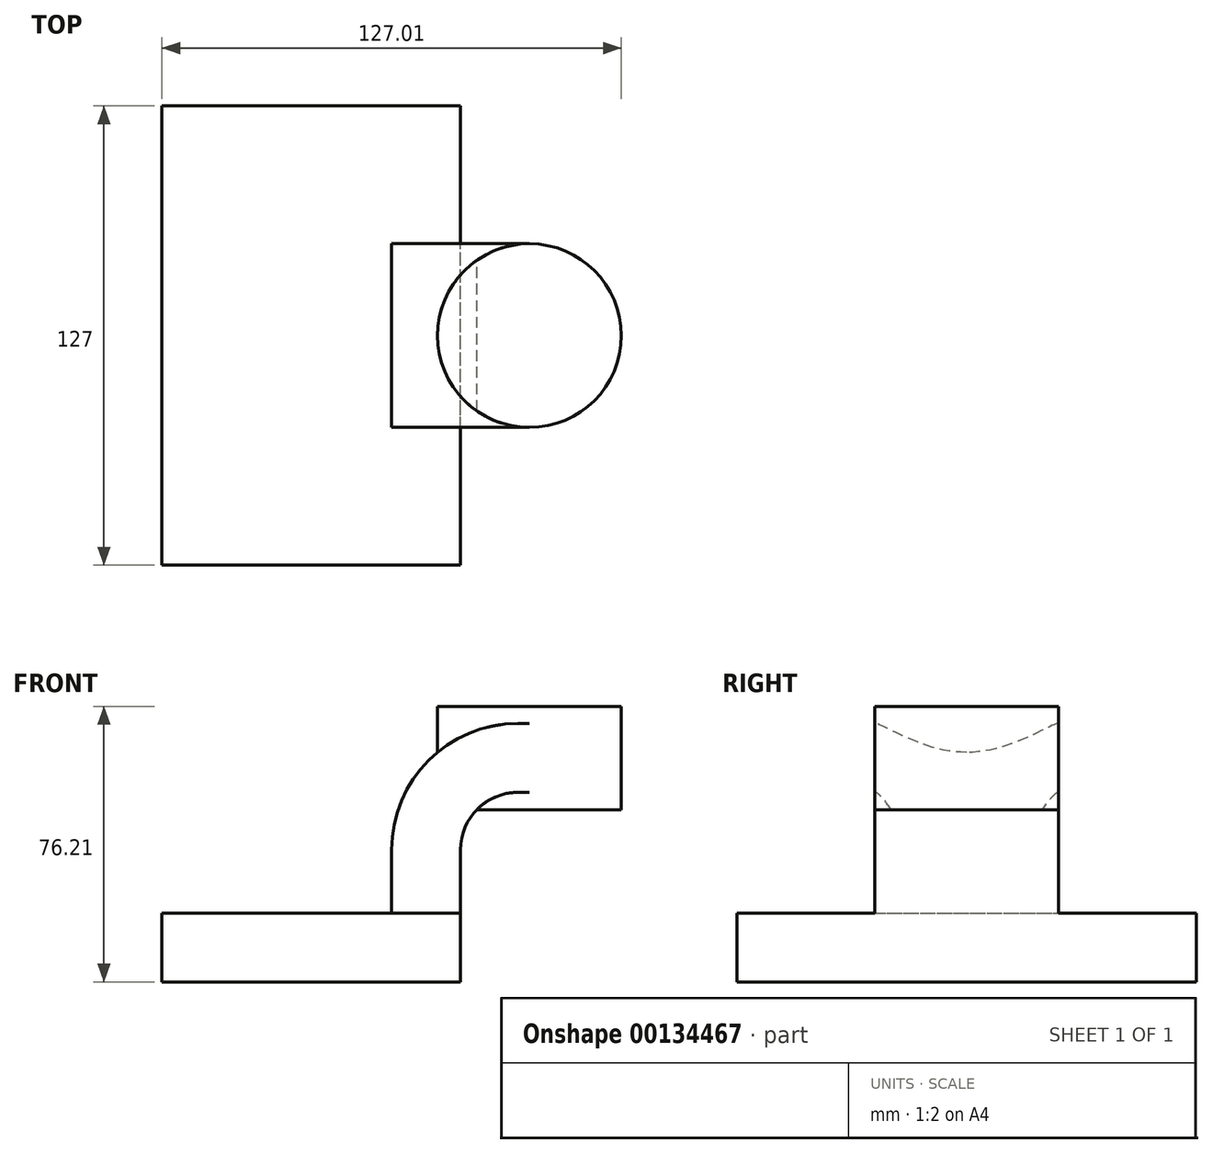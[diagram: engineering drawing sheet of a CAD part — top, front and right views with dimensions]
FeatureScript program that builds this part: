
annotation { "Feature Type Name" : "Feature", "Feature Type Description" : "" }
export const myFeature = defineFeature(function(context is Context, id is Id, definition is map)
    precondition{}
    {
        {
            var Q0;
            Q0=qCreatedBy(makeId("Front.planeOp"),FACE);
            var sketch = newSketch(context, id + "F0", { "sketchPlane" : qUnion([Q0])});
            skLineSegment(sketch, "E0.bottom", {"start": v(41.28, -9.53) * mm, "end": v(-41.28, -9.53) * mm});
            skLineSegment(sketch, "E0.top", {"start": v(41.27, 9.53) * mm, "end": v(-41.28, 9.53) * mm});
            skLineSegment(sketch, "E0.left", {"start": v(41.27, -9.53) * mm, "end": v(41.27, 9.53) * mm});
            skLineSegment(sketch, "E0.right", {"start": v(-41.28, -9.53) * mm, "end": v(-41.28, 9.52) * mm});
            skPoint(sketch, "E0.middle", {"position": v(0, 0) * mm});
            skLineSegment(sketch, "E1.bottom", {"start": v(111.12, 38.1) * mm, "end": v(60.33, 38.1) * mm});
            skLineSegment(sketch, "E1.top", {"start": v(111.12, 66.68) * mm, "end": v(60.33, 66.68) * mm});
            skLineSegment(sketch, "E1.left", {"start": v(111.13, 38.1) * mm, "end": v(111.13, 66.68) * mm});
            skLineSegment(sketch, "E1.right", {"start": v(60.33, 38.1) * mm, "end": v(60.33, 66.68) * mm});
            skLineSegment(sketch, "E2", {"start": v(41.27, 9.53) * mm, "end": v(41.27, 27) * mm});
            skArc(sketch, "E3", {"start": v(41.27, 27) * mm, "mid": v(45.92, 38.23) * mm, "end": v(57.15, 42.88) * mm});
            skLineSegment(sketch, "E4", {"start": v(57.15, 42.88) * mm, "end": v(85.73, 42.88) * mm});
            skLineSegment(sketch, "E5.0", {"start": v(57.15, 61.93) * mm, "end": v(85.72, 61.93) * mm});
            skArc(sketch, "E5.1", {"start": v(22.22, 27) * mm, "mid": v(32.45, 51.7) * mm, "end": v(57.15, 61.93) * mm});
            skLineSegment(sketch, "E6.0", {"start": v(22.22, 9.53) * mm, "end": v(22.22, 27) * mm});
            skFitSpline(sketch, "E7", {"points": [v(-41.28, 9.52) * mm, v(57.15, 61.93) * mm], "startDerivative": vector(-1.37, 29.96) * mm, "endDerivative": vector(193.18, -12.27) * mm});
            skLineSegment(sketch, "E8", {"start": v(85.72, 66.68) * mm, "end": v(85.72, 38.1) * mm});
            skSolve(sketch);
        }
        {
            var Q0;
            Q0=makeQuery(id+"F0.imprint","IMPRINT",FACE,{"disambiguationData":[TD([[makeQuery(id+"F0.imprint","IMPRINT",EDGE,{"derivedFrom":sQuery(id+"F0.wireOp",EDGE,"E0.bottom")}),-1.0]])]});
            extrude(context, id + "F1", {"entities" : qUnion([Q0]), "endBound" : BoundingType.SYMMETRIC, "depth" : 127 * mm});
        }
        {
            var Q0;
            {var subQ2=sQuery(id+"F0.wireOp",EDGE,"E2");Q0=makeQuery(id+"F0.imprint","IMPRINT",FACE,{"disambiguationData":[TD([[makeQuery(id+"F0.imprint","IMPRINT",EDGE,{"derivedFrom":subQ2}),1.0]])]});}
            var Q1;
            {var subQ5=sQuery(id+"F0.wireOp",EDGE,"xmvg7gtr-0cF6-FCa6-2jLr-h9ZZnqTFkXLl");Q1=makeQuery(id+"F0.imprint","IMPRINT",FACE,{"disambiguationData":[TD([[makeQuery(id+"F0.imprint","IMPRINT",EDGE,{"derivedFrom":subQ5}),-1.0]])]});}
            extrude(context, id + "F2", {"entities" : qUnion([Q0, Q1]), "operationType" : NewBodyOperationType.ADD, "endBound" : BoundingType.SYMMETRIC, "depth" : 50.8 * mm});
        }
        {
            var Q0;
            Q0=makeQuery(id+"F0.imprint","IMPRINT",FACE,{"disambiguationData":[TD([[makeQuery(id+"F0.imprint","IMPRINT",EDGE,{"derivedFrom":sQuery(id+"F0.wireOp",EDGE,"E5.1")}),1.0]])]});
            extrude(context, id + "F3", {"entities" : qUnion([Q0]), "operationType" : NewBodyOperationType.ADD, "endBound" : BoundingType.SYMMETRIC, "depth" : 15.88 * mm});
        }
        {
            var Q0;
            {var subQ0=sQuery(id+"F0.wireOp",EDGE,"E1.right");var subQ1=sQuery(id+"F0.wireOp",EDGE,"E1.top");var subQ2=makeQuery(id+"F0.imprint","INTERSECT",VERTEX,{"derivedFrom":[subQ1,subQ0]});Q0=makeQuery(id+"F0.imprint","IMPRINT",FACE,{"disambiguationData":[TD([[makeQuery(id+"F0.imprint","IMPRINT",EDGE,{"disambiguationData":[TD([[subQ2,1.0]])],"derivedFrom":subQ1}),1.0]])]});}
            var Q1;
            {var subQ0=sQuery(id+"F0.wireOp",EDGE,"E4");var subQ1=sQuery(id+"F0.wireOp",EDGE,"E1.right");var subQ2=makeQuery(id+"F0.imprint","INTERSECT",VERTEX,{"derivedFrom":[subQ1,subQ0]});Q1=makeQuery(id+"F0.imprint","IMPRINT",FACE,{"disambiguationData":[TD([[makeQuery(id+"F0.imprint","IMPRINT",EDGE,{"disambiguationData":[TD([[subQ2,-1.0]])],"derivedFrom":subQ1}),-1.0]])]});}
            var Q2;
            {var subQ0=sQuery(id+"F0.wireOp",EDGE,"E1.right");var subQ1=sQuery(id+"F0.wireOp",EDGE,"E1.bottom");var subQ2=makeQuery(id+"F0.imprint","INTERSECT",VERTEX,{"derivedFrom":[subQ1,subQ0]});Q2=makeQuery(id+"F0.imprint","IMPRINT",FACE,{"disambiguationData":[TD([[makeQuery(id+"F0.imprint","IMPRINT",EDGE,{"disambiguationData":[TD([[subQ2,1.0]])],"derivedFrom":subQ1}),-1.0]])]});}
            var Q3;
            Q3=sQuery(id+"F0.wireOp",EDGE,"E1.right");
            revolve(context, id + "F4", {"operationType" : NewBodyOperationType.ADD, "entities" : qUnion([Q0, Q1, Q2]), "axis" : qUnion([Q3]), "revolveType" : RevolveType.FULL});
        }
    });
